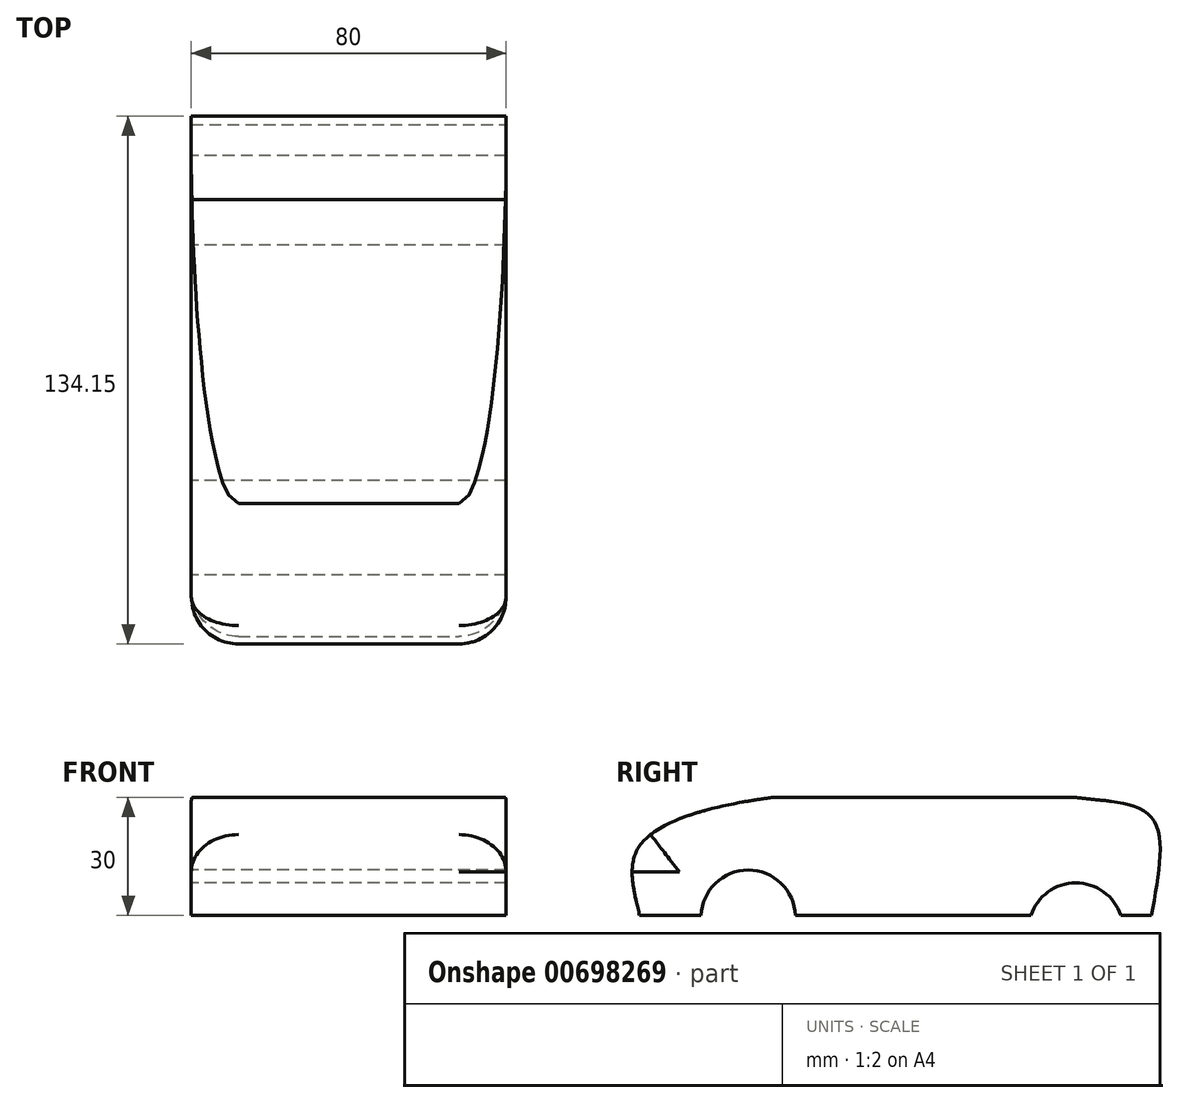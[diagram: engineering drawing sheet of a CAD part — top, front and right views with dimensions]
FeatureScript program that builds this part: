
annotation { "Feature Type Name" : "Feature", "Feature Type Description" : "" }
export const myFeature = defineFeature(function(context is Context, id is Id, definition is map)
    precondition{}
    {
        {
            var Q0;
            Q0=qCreatedBy(makeId("Top.planeOp"),FACE);
            var sketch = newSketch(context, id + "F0", { "sketchPlane" : qUnion([Q0])});
            skLineSegment(sketch, "E0.bottom", {"start": v(-40, -65) * mm, "end": v(40, -65) * mm});
            skLineSegment(sketch, "E0.top", {"start": v(-40, 65) * mm, "end": v(40, 65) * mm});
            skLineSegment(sketch, "E0.left", {"start": v(-40, -65) * mm, "end": v(-40, 65) * mm});
            skLineSegment(sketch, "E0.right", {"start": v(40, -65) * mm, "end": v(40, 65) * mm});
            skPoint(sketch, "E0.middle", {"position": v(0, 0) * mm});
            skSolve(sketch);
        }
        {
            var Q0;
            Q0=makeQuery(id+"F0.imprint","IMPRINT",FACE,{"disambiguationData":[TD([[makeQuery(id+"F0.imprint","IMPRINT",EDGE,{"derivedFrom":sQuery(id+"F0.wireOp",EDGE,"E0.bottom")}),1.0]])]});
            extrude(context, id + "F1", {"entities" : qUnion([Q0]), "depth" : 50 * mm, "offsetDistance" : 25 * mm});
        }
        {
            var Q0;
            Q0=makeQuery(id+"F1.opExtrude","SWEPT_FACE",FACE,{"disambiguationData":[OSD([sQuery(id+"F0.wireOp",EDGE,"E0.left")])]});
            var sketch = newSketch(context, id + "F2", { "sketchPlane" : qUnion([Q0])});
            skPoint(sketch, "E1", {"position": v(65, 17.75) * mm});
            skFitSpline(sketch, "E2", {"points": [v(65, 0) * mm, v(65, 17.75) * mm, v(31.21, 30) * mm], "startDerivative": vector(11.56, 47.3) * mm, "endDerivative": vector(-70.31, 9.08) * mm});
            skFitSpline(sketch, "E3", {"points": [v(-46, 30) * mm, v(-65, 25) * mm, v(-65, 0) * mm], "startDerivative": vector(-44.73, -6.51) * mm, "endDerivative": vector(9.87, -54.85) * mm});
            skLineSegment(sketch, "E4", {"start": v(-46, 30) * mm, "end": v(31.21, 30) * mm});
            skPoint(sketch, "E5", {"position": v(-44.95, 30) * mm});
            skLineSegment(sketch, "E6", {"start": v(-11.83, 31) * mm, "end": v(-10.64, 31) * mm});
            skPoint(sketch, "E7", {"position": v(-39.08, 48.05) * mm});
            skLineSegment(sketch, "E8", {"start": v(-46, 30) * mm, "end": v(-65, 30) * mm});
            skLineSegment(sketch, "E9", {"start": v(31.21, 30) * mm, "end": v(65, 30) * mm});
            skSolve(sketch);
        }
        {
            var Q0;
            Q0=makeQuery(id+"F2.imprint","IMPRINT",FACE,{"disambiguationData":[TD([[makeQuery(id+"F2.imprint","IMPRINT",EDGE,{"derivedFrom":sQuery(id+"F2.wireOp",EDGE,"E4")}),1.0]])]});
            var Q1;
            {var subQ0=sQuery(id+"F2.wireOp",EDGE,"E8");Q1=makeQuery(id+"F2.imprint","IMPRINT",FACE,{"disambiguationData":[TD([[makeQuery(id+"F2.imprint","IMPRINT",EDGE,{"derivedFrom":subQ0}),1.0]])]});}
            var Q2;
            {var subQ0=sQuery(id+"F2.wireOp",EDGE,"E9");Q2=makeQuery(id+"F2.imprint","IMPRINT",FACE,{"disambiguationData":[TD([[makeQuery(id+"F2.imprint","IMPRINT",EDGE,{"derivedFrom":subQ0}),-1.0]])]});}
            extrude(context, id + "F3", {"entities" : qUnion([Q0, Q1, Q2]), "operationType" : NewBodyOperationType.REMOVE, "oppositeDirection" : true, "depth" : 110.6 * mm, "offsetDistance" : 25 * mm});
        }
        {
            var Q0;
            {var subQ0=sQuery(id+"F2.wireOp",EDGE,"E3");var subQ1=sQuery(id+"F0.wireOp",EDGE,"E0.left");var subQ2=makeQuery(id+"F1.opExtrude","SWEPT_EDGE",EDGE,{"disambiguationData":[OSD([sQuery(id+"F0.wireOp",EDGE,"E0.top"),subQ1])]});var subQ4=makeQuery(id+"F2.imprint","INTERSECT",VERTEX,{"derivedFrom":[subQ2,subQ0]});Q0=makeQuery(id+"F2.imprint","IMPRINT",FACE,{"disambiguationData":[TD([[makeQuery(id+"F2.imprint","IMPRINT",EDGE,{"disambiguationData":[TD([[subQ4,-1.0]])],"derivedFrom":subQ0}),1.0]])]});}
            var Q1;
            {var subQ0=sQuery(id+"F2.wireOp",EDGE,"E2");var subQ1=sQuery(id+"F0.wireOp",EDGE,"E0.left");var subQ2=makeQuery(id+"F1.opExtrude","SWEPT_EDGE",EDGE,{"disambiguationData":[OSD([sQuery(id+"F0.wireOp",EDGE,"E0.bottom"),subQ1])]});var subQ4=makeQuery(id+"F2.imprint","INTERSECT",VERTEX,{"derivedFrom":[subQ2,subQ0]});Q1=makeQuery(id+"F2.imprint","IMPRINT",FACE,{"disambiguationData":[TD([[makeQuery(id+"F2.imprint","IMPRINT",EDGE,{"disambiguationData":[TD([[subQ4,1.0]])],"derivedFrom":subQ0}),1.0]])]});}
            extrude(context, id + "F4", {"entities" : qUnion([Q0, Q1]), "operationType" : NewBodyOperationType.ADD, "oppositeDirection" : true, "depth" : 80 * mm, "offsetDistance" : 25 * mm});
        }
        {
            var Q0;
            {var subQ0=sQuery(id+"F2.wireOp",EDGE,"E2");Q0=makeQuery(id+"F4.boolean.opBoolean","MERGE",EDGE,{"derivedFrom":[makeQuery(id+"F3.boolean.opBoolean","COPY",EDGE,{"derivedFrom":makeQuery(id+"F3.opExtrude","CAP_EDGE",EDGE,{"disambiguationData":[OSD([subQ0])],"isStart":true})}),makeQuery(id+"F4.opExtrude","CAP_EDGE",EDGE,{"disambiguationData":[OSD([subQ0])],"isStart":true})]});}
            fillet(context, id + "F5", {"entities" : qUnion([Q0]), "radius" : 12 * mm, "tangentPropagation" : true, "allowEdgeOverflow" : false});
        }
        {
            var Q0;
            {var subQ0=sQuery(id+"F2.wireOp",EDGE,"E2");Q0=makeQuery(id+"F4.boolean.opBoolean","MERGE",EDGE,{"derivedFrom":[makeQuery(id+"F3.boolean.opBoolean","INTERSECT",EDGE,{"derivedFrom":[makeQuery(id+"F1.opExtrude","SWEPT_FACE",FACE,{"disambiguationData":[OSD([sQuery(id+"F0.wireOp",EDGE,"E0.right")])]}),makeQuery(id+"F3.opExtrude","SWEPT_FACE",FACE,{"disambiguationData":[OSD([subQ0])]})]}),makeQuery(id+"F4.opExtrude","CAP_EDGE",EDGE,{"disambiguationData":[OSD([subQ0])],"isStart":false})]});}
            fillet(context, id + "F6", {"entities" : qUnion([Q0]), "radius" : 12 * mm, "tangentPropagation" : true, "allowEdgeOverflow" : false});
        }
        {
            var Q0;
            {var subQ0=sQuery(id+"F0.wireOp",EDGE,"E0.left");Q0=makeQuery(id+"F4.boolean.opBoolean","MERGE",FACE,{"derivedFrom":[makeQuery(id+"F1.opExtrude","SWEPT_FACE",FACE,{"disambiguationData":[OSD([subQ0])]}),makeQuery(id+"F4.opExtrude","CAP_FACE",FACE,{"disambiguationData":[OSD([sQuery(id+"F0.wireOp",EDGE,"E0.bottom"),subQ0,sQuery(id+"F2.wireOp",EDGE,"E2")])],"isStart":true}),makeQuery(id+"F4.opExtrude","CAP_FACE",FACE,{"disambiguationData":[OSD([sQuery(id+"F0.wireOp",EDGE,"E0.top"),subQ0,sQuery(id+"F2.wireOp",EDGE,"E3")])],"isStart":true})]});}
            var sketch = newSketch(context, id + "F7", { "sketchPlane" : qUnion([Q0])});
            skArc(sketch, "E10", {"start": v(49.4, 0) * mm, "mid": v(37.41, 11.55) * mm, "end": v(25.42, 0) * mm});
            skArc(sketch, "E11", {"start": v(-34.39, 0) * mm, "mid": v(-45.8, 8.3) * mm, "end": v(-57.22, 0) * mm});
            skSolve(sketch);
        }
        {
            var Q0;
            {var subQ0=sQuery(id+"F7.wireOp",EDGE,"E11");Q0=makeQuery(id+"F7.imprint","IMPRINT",FACE,{"disambiguationData":[TD([[makeQuery(id+"F7.imprint","IMPRINT",EDGE,{"derivedFrom":subQ0}),1.0]])]});}
            var Q1;
            {var subQ0=sQuery(id+"F7.wireOp",EDGE,"E10");Q1=makeQuery(id+"F7.imprint","IMPRINT",FACE,{"disambiguationData":[TD([[makeQuery(id+"F7.imprint","IMPRINT",EDGE,{"derivedFrom":subQ0}),1.0]])]});}
            extrude(context, id + "F8", {"entities" : qUnion([Q0, Q1]), "operationType" : NewBodyOperationType.REMOVE, "oppositeDirection" : true, "depth" : 96.7 * mm, "offsetDistance" : 25 * mm});
        }
    });
